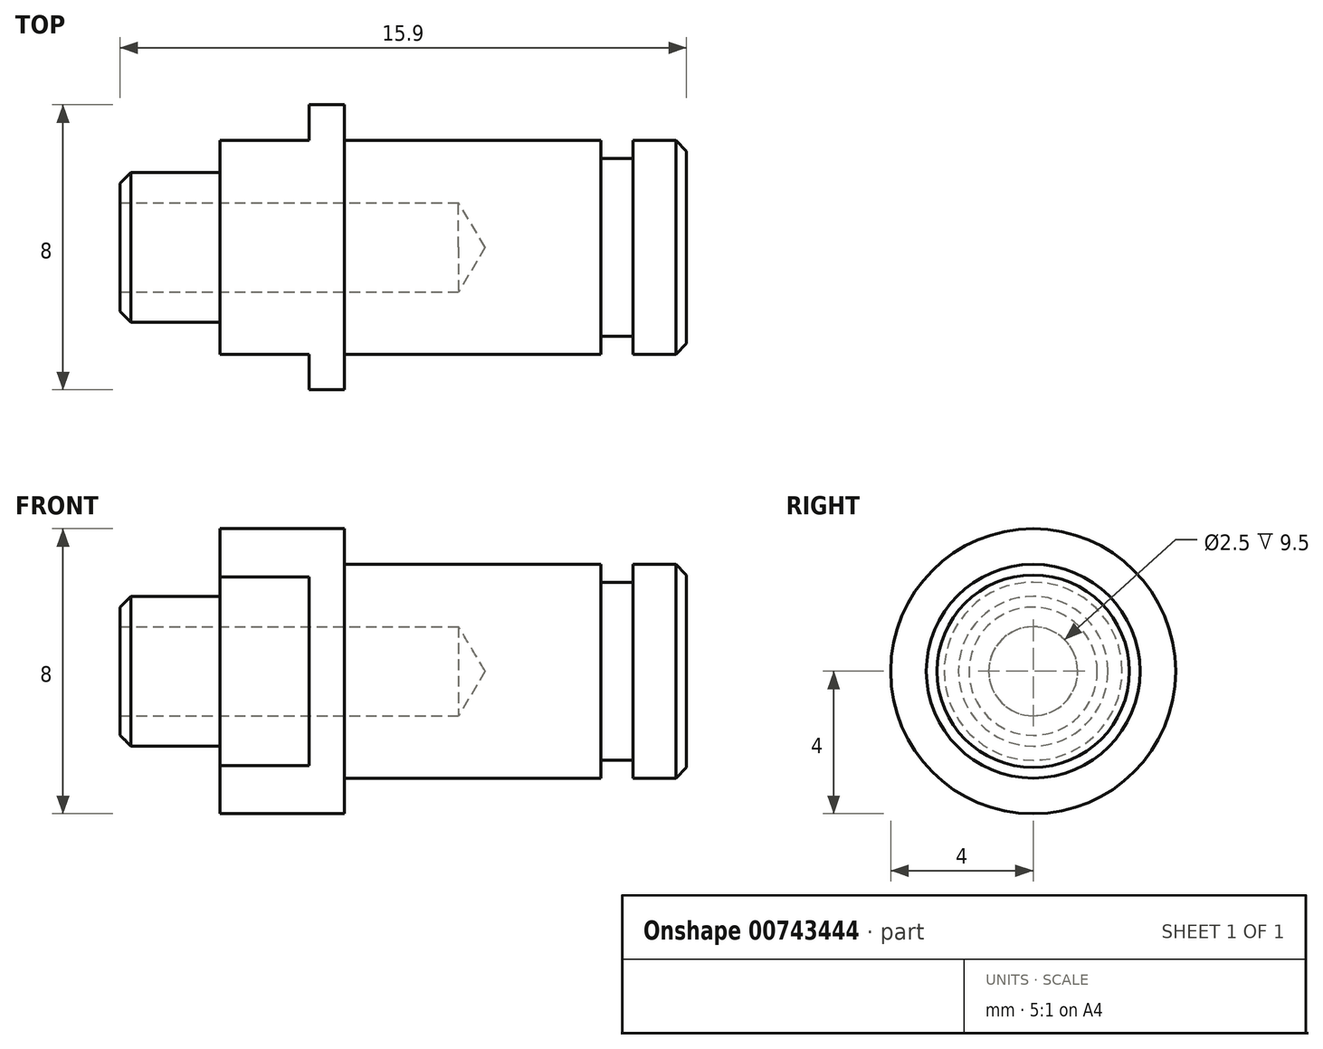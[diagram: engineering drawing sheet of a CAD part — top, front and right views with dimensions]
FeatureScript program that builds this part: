
annotation { "Feature Type Name" : "Feature", "Feature Type Description" : "" }
export const myFeature = defineFeature(function(context is Context, id is Id, definition is map)
    precondition{}
    {
        {
            var Q0;
            Q0=qCreatedBy(makeId("Front.planeOp"),FACE);
            var sketch = newSketch(context, id + "F0", { "sketchPlane" : qUnion([Q0])});
            skLineSegment(sketch, "E0", {"start": v(-5.93, 0) * mm, "end": v(-5.93, 2.1) * mm});
            skLineSegment(sketch, "E1", {"start": v(-5.93, 2.1) * mm, "end": v(-3.13, 2.1) * mm});
            skLineSegment(sketch, "E2", {"start": v(-3.13, 2.1) * mm, "end": v(-3.13, 4) * mm});
            skLineSegment(sketch, "E3", {"start": v(-3.13, 4) * mm, "end": v(0.37, 4) * mm});
            skLineSegment(sketch, "E4", {"start": v(0.37, 4) * mm, "end": v(0.37, 3) * mm});
            skLineSegment(sketch, "E5", {"start": v(0.37, 3) * mm, "end": v(9.97, 3) * mm});
            skLineSegment(sketch, "E6", {"start": v(9.97, 3) * mm, "end": v(9.97, 0) * mm});
            skLineSegment(sketch, "E7", {"start": v(9.97, 0) * mm, "end": v(-5.93, 0) * mm});
            skSolve(sketch);
        }
        {
            var Q0;
            Q0=qSketchRegion(id+"F0",true);
            var Q1;
            Q1=sQuery(id+"F0.wireOp",EDGE,"E7");
            revolve(context, id + "F1", {"entities" : qUnion([Q0]), "axis" : qUnion([Q1]), "revolveType" : RevolveType.FULL});
        }
        {
            var Q0;
            Q0=makeQuery(id+"F1.opRevolve","SWEPT_FACE",FACE,{"disambiguationData":[OSD([sQuery(id+"F0.wireOp",EDGE,"E2")])]});
            var sketch = newSketch(context, id + "F2", { "sketchPlane" : qUnion([Q0])});
            skLineSegment(sketch, "E8.bottom", {"start": v(3, 5) * mm, "end": v(7, 5) * mm});
            skLineSegment(sketch, "E8.top", {"start": v(3, -5) * mm, "end": v(7, -5) * mm});
            skLineSegment(sketch, "E8.left", {"start": v(3, 5) * mm, "end": v(3, -5) * mm});
            skLineSegment(sketch, "E8.right", {"start": v(7, 5) * mm, "end": v(7, -5) * mm});
            skLineSegment(sketch, "E9.bottom", {"start": v(-3, 5) * mm, "end": v(-7, 5) * mm});
            skLineSegment(sketch, "E9.top", {"start": v(-3, -5) * mm, "end": v(-7, -5) * mm});
            skLineSegment(sketch, "E9.left", {"start": v(-3, 5) * mm, "end": v(-3, -5) * mm});
            skLineSegment(sketch, "E9.right", {"start": v(-7, 5) * mm, "end": v(-7, -5) * mm});
            skSolve(sketch);
        }
        {
            var Q0;
            Q0=qSketchRegion(id+"F2",true);
            extrude(context, id + "F3", {"entities" : qUnion([Q0]), "operationType" : NewBodyOperationType.REMOVE, "oppositeDirection" : true, "depth" : 2.5 * mm, "offsetDistance" : 25 * mm});
        }
        {
            var Q0;
            Q0=makeQuery(id+"F1.opRevolve","SWEPT_FACE",FACE,{"disambiguationData":[OSD([sQuery(id+"F0.wireOp",EDGE,"E0")])]});
            var sketch = newSketch(context, id + "F4", { "sketchPlane" : qUnion([Q0])});
            skPoint(sketch, "E10", {"position": v(0, 0) * mm});
            skSolve(sketch);
        }
        {
            var Q0;
            Q0=sQuery(id+"F4.wireOp",VERTEX,"E10");
            var Q1;
            Q1=makeQuery(id+"F1.opRevolve","SWEPT_BODY",BODY,{"disambiguationData":[OSD([sQuery(id+"F0.wireOp",EDGE,"E0"),sQuery(id+"F0.wireOp",EDGE,"E1"),sQuery(id+"F0.wireOp",EDGE,"E2"),sQuery(id+"F0.wireOp",EDGE,"E3"),sQuery(id+"F0.wireOp",EDGE,"E4"),sQuery(id+"F0.wireOp",EDGE,"E5"),sQuery(id+"F0.wireOp",EDGE,"E6"),sQuery(id+"F0.wireOp",EDGE,"E7")])]});
            hole(context, id + "F5", {"style" : HoleStyle.SIMPLE, "endStyle" : HoleEndStyle.BLIND, "standardTappedOrClearance" : lookupTablePath({ "standard" : "ISO", "engagement" : "75%", "pitch" : "0.5 mm", "size" : "M3", "type" : "Tapped" }), "standardBlindInLast" : lookupTablePath({ "standard" : "ISO", "engagement" : "75%", "pitch" : "0.5 mm", "size" : "M3", "type" : "Tapped" }), "holeDiameter" : 2.5 * mm, "majorDiameter" : 3 * mm, "showTappedDepth" : true, "holeDepth" : 9.5 * mm, "tappedDepth" : 8 * mm, "tapClearance" : 3, "locations" : qUnion([Q0]), "scope" : qUnion([Q1]), "startStyle" : HoleStartStyle.SKETCH});
        }
        {
            var Q0;
            Q0=qCreatedBy(makeId("Front.planeOp"),FACE);
            var sketch = newSketch(context, id + "F6", { "sketchPlane" : qUnion([Q0])});
            skLineSegment(sketch, "E11.bottom", {"start": v(7.57, 4.5) * mm, "end": v(8.47, 4.5) * mm});
            skLineSegment(sketch, "E11.top", {"start": v(7.57, 2.5) * mm, "end": v(8.47, 2.5) * mm});
            skLineSegment(sketch, "E11.left", {"start": v(7.57, 4.5) * mm, "end": v(7.57, 2.5) * mm});
            skLineSegment(sketch, "E11.right", {"start": v(8.47, 4.5) * mm, "end": v(8.47, 2.5) * mm});
            skSolve(sketch);
        }
        {
            var Q0;
            Q0=qSketchRegion(id+"F6",true);
            var Q1;
            Q1=sQuery(id+"F0.wireOp",EDGE,"E7");
            revolve(context, id + "F7", {"operationType" : NewBodyOperationType.REMOVE, "entities" : qUnion([Q0]), "axis" : qUnion([Q1]), "revolveType" : RevolveType.FULL, "oppositeDirection" : true});
        }
        {
            var Q0;
            Q0=makeQuery(id+"F1.opRevolve","SWEPT_EDGE",EDGE,{"disambiguationData":[OSD([sQuery(id+"F0.wireOp",EDGE,"E5"),sQuery(id+"F0.wireOp",EDGE,"E6")])]});
            var Q1;
            Q1=makeQuery(id+"F1.opRevolve","SWEPT_EDGE",EDGE,{"disambiguationData":[OSD([sQuery(id+"F0.wireOp",EDGE,"E0"),sQuery(id+"F0.wireOp",EDGE,"E1")])]});
            chamfer(context, id + "F8", {"entities" : qUnion([Q0, Q1]), "width" : 0.3 * mm, "tangentPropagation" : true});
        }
    });
